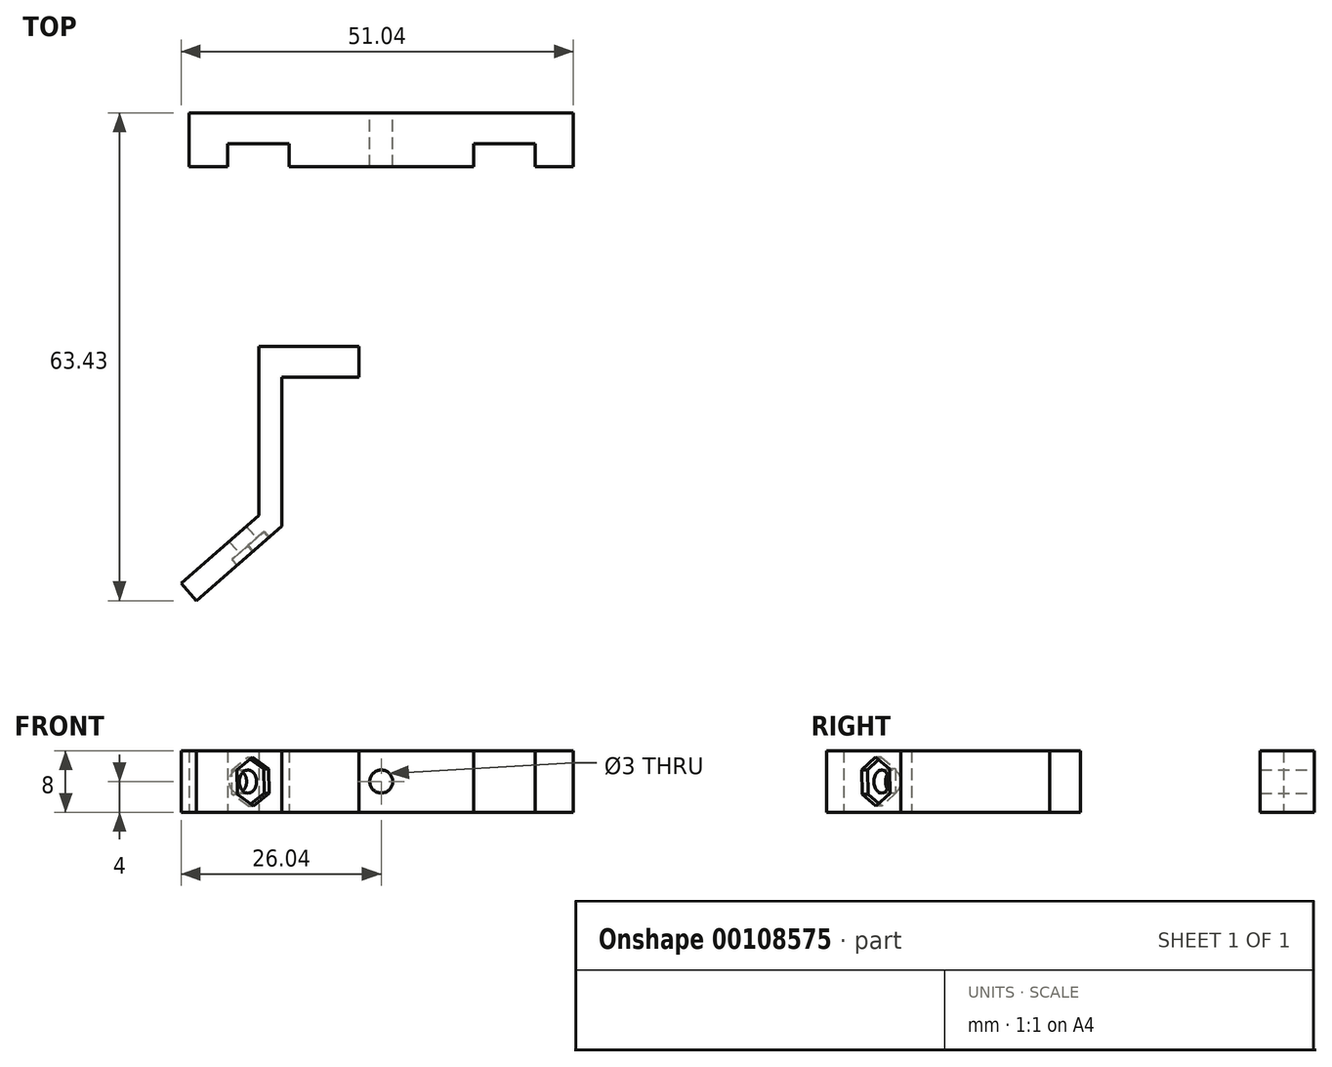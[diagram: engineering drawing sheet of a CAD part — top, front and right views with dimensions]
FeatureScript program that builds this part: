
annotation { "Feature Type Name" : "Feature", "Feature Type Description" : "" }
export const myFeature = defineFeature(function(context is Context, id is Id, definition is map)
    precondition{}
    {
        {
            var Q0;
            Q0=qCreatedBy(makeId("Top.planeOp"),FACE);
            var sketch = newSketch(context, id + "F0", { "sketchPlane" : qUnion([Q0])});
            skLineSegment(sketch, "E0", {"start": v(0.74, 15.94) * mm, "end": v(-12.26, 15.94) * mm});
            skLineSegment(sketch, "E1", {"start": v(-12.26, 15.94) * mm, "end": v(-12.26, -6.06) * mm});
            skLineSegment(sketch, "E2", {"start": v(-9.26, -7.42) * mm, "end": v(-9.26, 11.94) * mm});
            skLineSegment(sketch, "E3", {"start": v(-9.26, 11.94) * mm, "end": v(0.74, 11.94) * mm});
            skLineSegment(sketch, "E4", {"start": v(0.74, 15.94) * mm, "end": v(0.74, 11.94) * mm});
            skLineSegment(sketch, "E5", {"start": v(-12.26, -6.06) * mm, "end": v(-22.38, -14.87) * mm});
            skLineSegment(sketch, "E6", {"start": v(-22.38, -14.87) * mm, "end": v(-20.4, -17.13) * mm});
            skLineSegment(sketch, "E7", {"start": v(-20.4, -17.13) * mm, "end": v(-9.26, -7.42) * mm});
            skSolve(sketch);
        }
        {
            var Q0;
            Q0=makeQuery(id+"F0.imprint","IMPRINT",FACE,{"disambiguationData":[TD([[makeQuery(id+"F0.imprint","IMPRINT",EDGE,{"derivedFrom":sQuery(id+"F0.wireOp",EDGE,"E0")}),1.0]])]});
            extrude(context, id + "F1", {"entities" : qUnion([Q0]), "depth" : 8 * mm});
        }
        {
            var Q0;
            Q0=makeQuery(id+"F1.opExtrude","SWEPT_FACE",FACE,{"disambiguationData":[OSD([sQuery(id+"F0.wireOp",EDGE,"E7")])]});
            var sketch = newSketch(context, id + "F2", { "sketchPlane" : qUnion([Q0])});
            skCircle(sketch, "E8", {"center": v(-16.86, 4) * mm, "radius": 1.5 * mm});
            skCircle(sketch, "E9.cCircle", {"center": v(-16.86, 4) * mm, "radius": 2.75 * mm, "construction": true});
            skLineSegment(sketch, "E9.0", {"start": v(-16.93, 7.17) * mm, "end": v(-14.14, 5.65) * mm});
            skLineSegment(sketch, "E9.1", {"start": v(-14.14, 5.65) * mm, "end": v(-14.07, 2.47) * mm});
            skLineSegment(sketch, "E9.2", {"start": v(-14.07, 2.47) * mm, "end": v(-16.78, 0.83) * mm});
            skLineSegment(sketch, "E9.3", {"start": v(-16.78, 0.83) * mm, "end": v(-19.57, 2.35) * mm});
            skLineSegment(sketch, "E9.4", {"start": v(-19.57, 2.35) * mm, "end": v(-19.64, 5.53) * mm});
            skLineSegment(sketch, "E9.5", {"start": v(-19.64, 5.53) * mm, "end": v(-16.93, 7.17) * mm});
            skPoint(sketch, "E9.0.midPoint", {"position": v(-15.53, 6.41) * mm});
            skSolve(sketch);
        }
        {
            var Q0;
            Q0=makeQuery(id+"F2.imprint","IMPRINT",FACE,{"disambiguationData":[TD([[makeQuery(id+"F2.imprint","IMPRINT",EDGE,{"derivedFrom":sQuery(id+"F2.wireOp",EDGE,"E8")}),1.0]])]});
            extrude(context, id + "F3", {"entities" : qUnion([Q0]), "operationType" : NewBodyOperationType.REMOVE, "oppositeDirection" : true, "depth" : 25 * mm});
        }
        {
            var Q0;
            Q0=makeQuery(id+"F2.imprint","IMPRINT",FACE,{"disambiguationData":[TD([[makeQuery(id+"F2.imprint","IMPRINT",EDGE,{"derivedFrom":sQuery(id+"F2.wireOp",EDGE,"E8")}),-1.0]])]});
            extrude(context, id + "F4", {"entities" : qUnion([Q0]), "operationType" : NewBodyOperationType.REMOVE, "oppositeDirection" : true, "depth" : 1 * mm});
        }
        {
            var Q0;
            Q0=qCreatedBy(makeId("Top.planeOp"),FACE);
            var sketch = newSketch(context, id + "F5", { "sketchPlane" : qUnion([Q0])});
            skLineSegment(sketch, "E10.bottom", {"start": v(-21.34, 46.3) * mm, "end": v(28.66, 46.3) * mm});
            skLineSegment(sketch, "E10.top", {"start": v(-21.34, 39.3) * mm, "end": v(28.66, 39.3) * mm});
            skLineSegment(sketch, "E10.left", {"start": v(-21.34, 46.3) * mm, "end": v(-21.34, 39.3) * mm});
            skLineSegment(sketch, "E10.right", {"start": v(28.66, 46.3) * mm, "end": v(28.66, 39.3) * mm});
            skPoint(sketch, "E11.oppositeSnap0", {"position": v(-21.34, 42.8) * mm});
            skLineSegment(sketch, "E12.bottom", {"start": v(-16.34, 39.3) * mm, "end": v(-8.34, 39.3) * mm});
            skLineSegment(sketch, "E12.top", {"start": v(-16.34, 42.3) * mm, "end": v(-8.34, 42.3) * mm});
            skLineSegment(sketch, "E12.left", {"start": v(-16.34, 39.3) * mm, "end": v(-16.34, 42.3) * mm});
            skLineSegment(sketch, "E12.right", {"start": v(-8.34, 39.3) * mm, "end": v(-8.34, 42.3) * mm});
            skLineSegment(sketch, "E13.bottom", {"start": v(23.66, 39.3) * mm, "end": v(15.66, 39.3) * mm});
            skLineSegment(sketch, "E13.top", {"start": v(23.66, 42.3) * mm, "end": v(15.66, 42.3) * mm});
            skLineSegment(sketch, "E13.left", {"start": v(23.66, 39.3) * mm, "end": v(23.66, 42.3) * mm});
            skLineSegment(sketch, "E13.right", {"start": v(15.66, 39.3) * mm, "end": v(15.66, 42.3) * mm});
            skSolve(sketch);
        }
        {
            var Q0;
            Q0=makeQuery(id+"F5.imprint","IMPRINT",FACE,{"disambiguationData":[TD([[makeQuery(id+"F5.imprint","IMPRINT",EDGE,{"derivedFrom":sQuery(id+"F5.wireOp",EDGE,"E10.bottom")}),-1.0]])]});
            extrude(context, id + "F6", {"entities" : qUnion([Q0]), "depth" : 8 * mm});
        }
        {
            var Q0;
            Q0=makeQuery(id+"F6.opExtrude","SWEPT_FACE",FACE,{"disambiguationData":[OSD([sQuery(id+"F5.wireOp",EDGE,"E10.bottom")])]});
            var sketch = newSketch(context, id + "F7", { "sketchPlane" : qUnion([Q0])});
            skCircle(sketch, "E14", {"center": v(-3.66, 4) * mm, "radius": 1.5 * mm});
            skSolve(sketch);
        }
        {
            var Q0;
            Q0=makeQuery(id+"F7.imprint","IMPRINT",FACE,{"disambiguationData":[TD([[makeQuery(id+"F7.imprint","IMPRINT",EDGE,{"derivedFrom":sQuery(id+"F7.wireOp",EDGE,"E14")}),1.0]])]});
            extrude(context, id + "F8", {"entities" : qUnion([Q0]), "operationType" : NewBodyOperationType.REMOVE, "oppositeDirection" : true, "depth" : 25 * mm});
        }
    });
